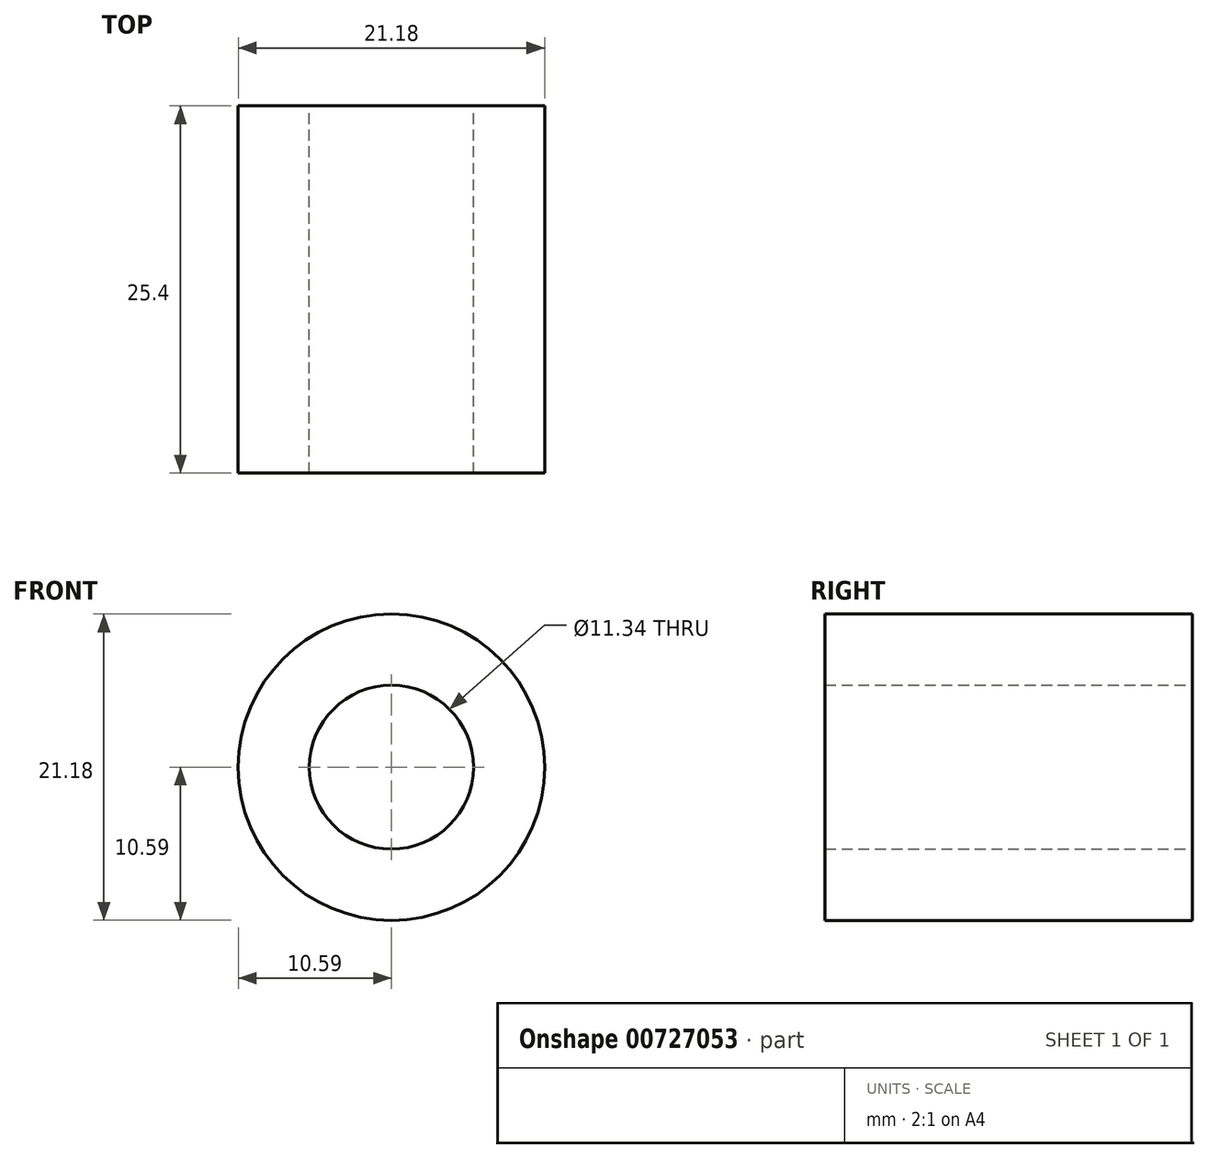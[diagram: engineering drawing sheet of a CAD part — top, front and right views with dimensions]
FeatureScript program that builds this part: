
annotation { "Feature Type Name" : "Feature", "Feature Type Description" : "" }
export const myFeature = defineFeature(function(context is Context, id is Id, definition is map)
    precondition{}
    {
        {
            var Q0;
            Q0=qCreatedBy(makeId("Front.planeOp"),FACE);
            var sketch = newSketch(context, id + "F0", { "sketchPlane" : qUnion([Q0])});
            skCircle(sketch, "E0", {"center": v(0, 0) * mm, "radius": 10.6 * mm});
            skCircle(sketch, "E1", {"center": v(0, 0) * mm, "radius": 5.67 * mm});
            skSolve(sketch);
        }
        {
            var Q0;
            Q0=sQuery(id+"F0.wireOp",EDGE,"E1");
            extrude(context, id + "F1", {"bodyType" : ToolBodyType.SURFACE, "surfaceEntities" : qUnion([Q0]), "depth" : 140.2 * mm, "offsetDistance" : 25.4 * mm});
        }
        {
            var Q0;
            Q0 = qSketchRegion(id + "F0", true);
            extrude(context, id + "F2", {"entities" : qUnion([Q0]), "depth" : 25.4 * mm, "offsetDistance" : 25.4 * mm});
        }
    });
